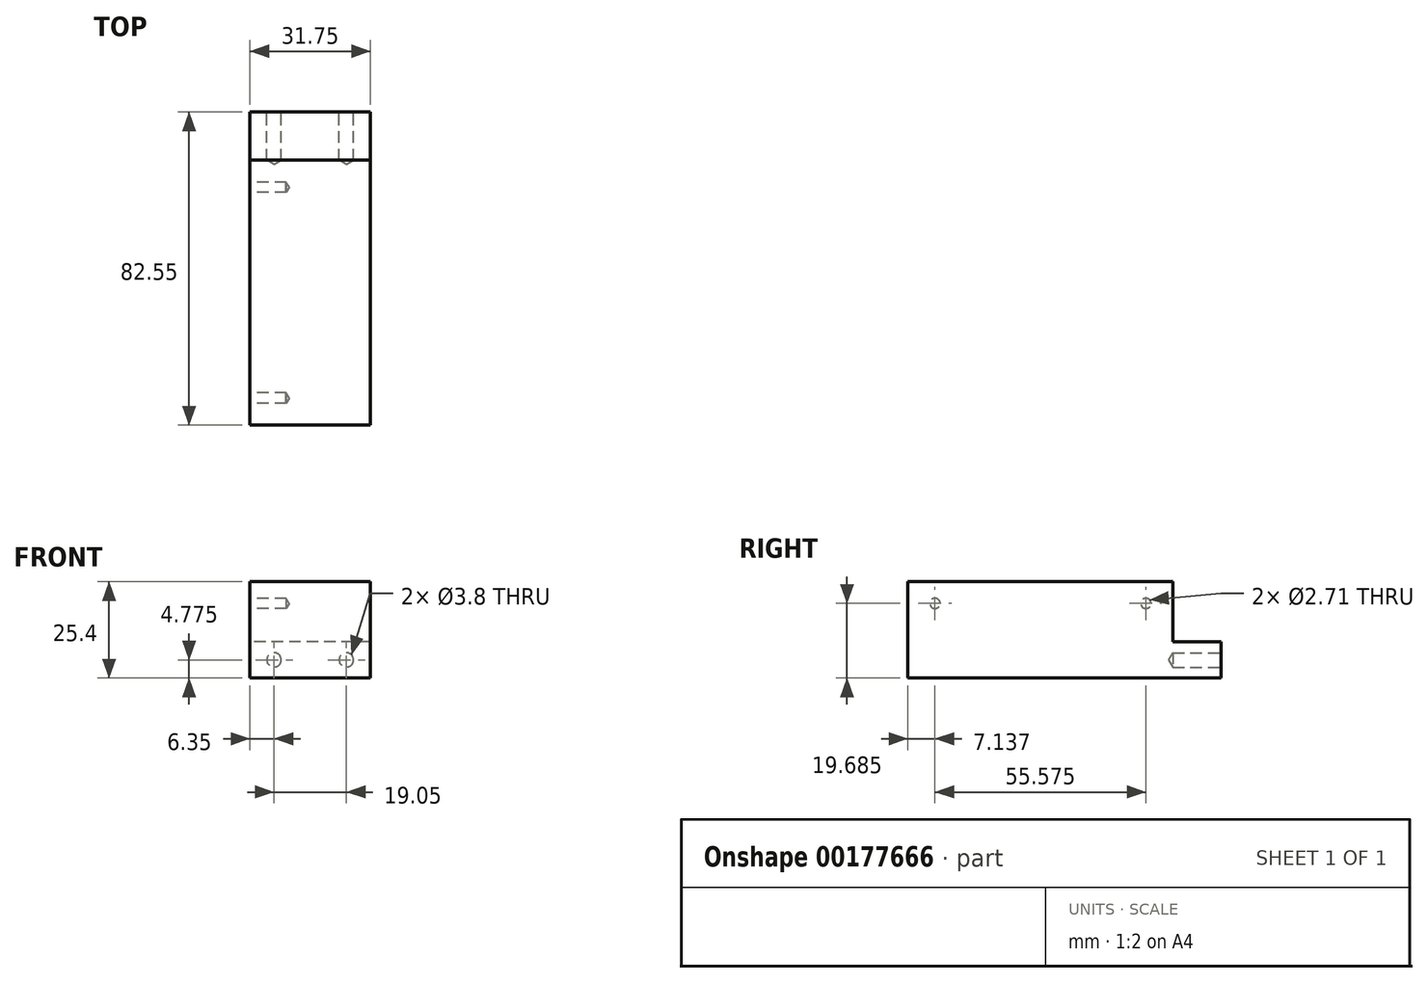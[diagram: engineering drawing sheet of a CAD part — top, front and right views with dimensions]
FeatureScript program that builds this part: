
annotation { "Feature Type Name" : "Feature", "Feature Type Description" : "" }
export const myFeature = defineFeature(function(context is Context, id is Id, definition is map)
    precondition{}
    {
        {
            var Q0;
            Q0=qCreatedBy(makeId("Top.planeOp"),FACE);
            var sketch = newSketch(context, id + "F0", { "sketchPlane" : qUnion([Q0])});
            skLineSegment(sketch, "E0.bottom", {"start": v(0, 0) * mm, "end": v(31.75, 0) * mm});
            skLineSegment(sketch, "E0.top", {"start": v(0, -82.55) * mm, "end": v(31.75, -82.55) * mm});
            skLineSegment(sketch, "E0.left", {"start": v(0, 0) * mm, "end": v(0, -82.55) * mm});
            skLineSegment(sketch, "E0.right", {"start": v(31.75, 0) * mm, "end": v(31.75, -82.55) * mm});
            skSolve(sketch);
        }
        {
            var Q0;
            Q0=qSketchRegion(id+"F0",true);
            extrude(context, id + "F1", {"entities" : qUnion([Q0]), "depth" : 25.4 * mm});
        }
        {
            var Q0;
            Q0=makeQuery(id+"F1.opExtrude","SWEPT_FACE",FACE,{"disambiguationData":[OSD([sQuery(id+"F0.wireOp",EDGE,"E0.bottom")])]});
            var sketch = newSketch(context, id + "F2", { "sketchPlane" : qUnion([Q0])});
            skLineSegment(sketch, "E1.bottom", {"start": v(-31.75, 25.4) * mm, "end": v(0, 25.4) * mm});
            skLineSegment(sketch, "E1.top", {"start": v(-31.75, 9.53) * mm, "end": v(0, 9.53) * mm});
            skLineSegment(sketch, "E1.left", {"start": v(-31.75, 25.4) * mm, "end": v(-31.75, 9.53) * mm});
            skLineSegment(sketch, "E1.right", {"start": v(0, 25.4) * mm, "end": v(0, 9.53) * mm});
            skSolve(sketch);
        }
        {
            var Q0;
            Q0=qSketchRegion(id+"F2",true);
            extrude(context, id + "F3", {"entities" : qUnion([Q0]), "operationType" : NewBodyOperationType.REMOVE, "oppositeDirection" : true, "depth" : 12.7 * mm});
        }
        {
            var Q0;
            Q0=makeQuery(id+"F1.opExtrude","SWEPT_FACE",FACE,{"disambiguationData":[OSD([sQuery(id+"F0.wireOp",EDGE,"E0.bottom")])]});
            var sketch = newSketch(context, id + "F4", { "sketchPlane" : qUnion([Q0])});
            skPoint(sketch, "E2", {"position": v(-25.4, 4.78) * mm});
            skPoint(sketch, "E3", {"position": v(-6.35, 4.78) * mm});
            skSolve(sketch);
        }
        {
            var Q0;
            Q0=sQuery(id+"F4.wireOp",VERTEX,"E2");
            var Q1;
            Q1=sQuery(id+"F4.wireOp",VERTEX,"E3");
            var Q2;
            Q2=makeQuery(id+"F1.opExtrude","SWEPT_BODY",BODY,{"disambiguationData":[OSD([sQuery(id+"F0.wireOp",EDGE,"E0.bottom"),sQuery(id+"F0.wireOp",EDGE,"E0.top"),sQuery(id+"F0.wireOp",EDGE,"E0.left"),sQuery(id+"F0.wireOp",EDGE,"E0.right")])]});
            hole(context, id + "F5", {"style" : HoleStyle.SIMPLE, "endStyle" : HoleEndStyle.BLIND, "standardTappedOrClearance" : lookupTablePath({ "standard" : "ANSI", "engagement" : "75%", "pitch" : "24 tpi", "size" : "#10", "type" : "Tapped" }), "standardBlindInLast" : lookupTablePath({ "standard" : "ANSI", "engagement" : "75%", "pitch" : "24 tpi", "size" : "#10", "type" : "Tapped" }), "holeDiameter" : 3.8 * mm, "holeDepth" : 12.7 * mm, "startFromSketch" : true, "locations" : qUnion([Q0, Q1]), "scope" : qUnion([Q2]), "majorDiameter" : 4.83 * mm});
        }
        {
            var Q0;
            Q0=makeQuery(id+"F1.opExtrude","SWEPT_FACE",FACE,{"disambiguationData":[OSD([sQuery(id+"F0.wireOp",EDGE,"E0.left")])]});
            var sketch = newSketch(context, id + "F6", { "sketchPlane" : qUnion([Q0])});
            skPoint(sketch, "E4", {"position": v(19.84, 19.69) * mm});
            skPoint(sketch, "E5", {"position": v(75.41, 19.69) * mm});
            skSolve(sketch);
        }
        {
            var Q0;
            Q0=sQuery(id+"F6.wireOp",VERTEX,"E4");
            var Q1;
            Q1=sQuery(id+"F6.wireOp",VERTEX,"E5");
            var Q2;
            Q2=makeQuery(id+"F1.opExtrude","SWEPT_BODY",BODY,{"disambiguationData":[OSD([sQuery(id+"F0.wireOp",EDGE,"E0.bottom"),sQuery(id+"F0.wireOp",EDGE,"E0.top"),sQuery(id+"F0.wireOp",EDGE,"E0.left"),sQuery(id+"F0.wireOp",EDGE,"E0.right")])]});
            hole(context, id + "F7", {"style" : HoleStyle.SIMPLE, "endStyle" : HoleEndStyle.BLIND, "standardTappedOrClearance" : lookupTablePath({ "standard" : "ANSI", "engagement" : "75%", "pitch" : "32 tpi", "size" : "#6", "type" : "Tapped" }), "standardBlindInLast" : lookupTablePath({ "standard" : "ANSI", "engagement" : "75%", "pitch" : "32 tpi", "size" : "#6", "type" : "Tapped" }), "holeDiameter" : 2.7 * mm, "holeDepth" : 9.52 * mm, "startFromSketch" : true, "locations" : qUnion([Q0, Q1]), "scope" : qUnion([Q2]), "majorDiameter" : 3.5 * mm});
        }
    });
